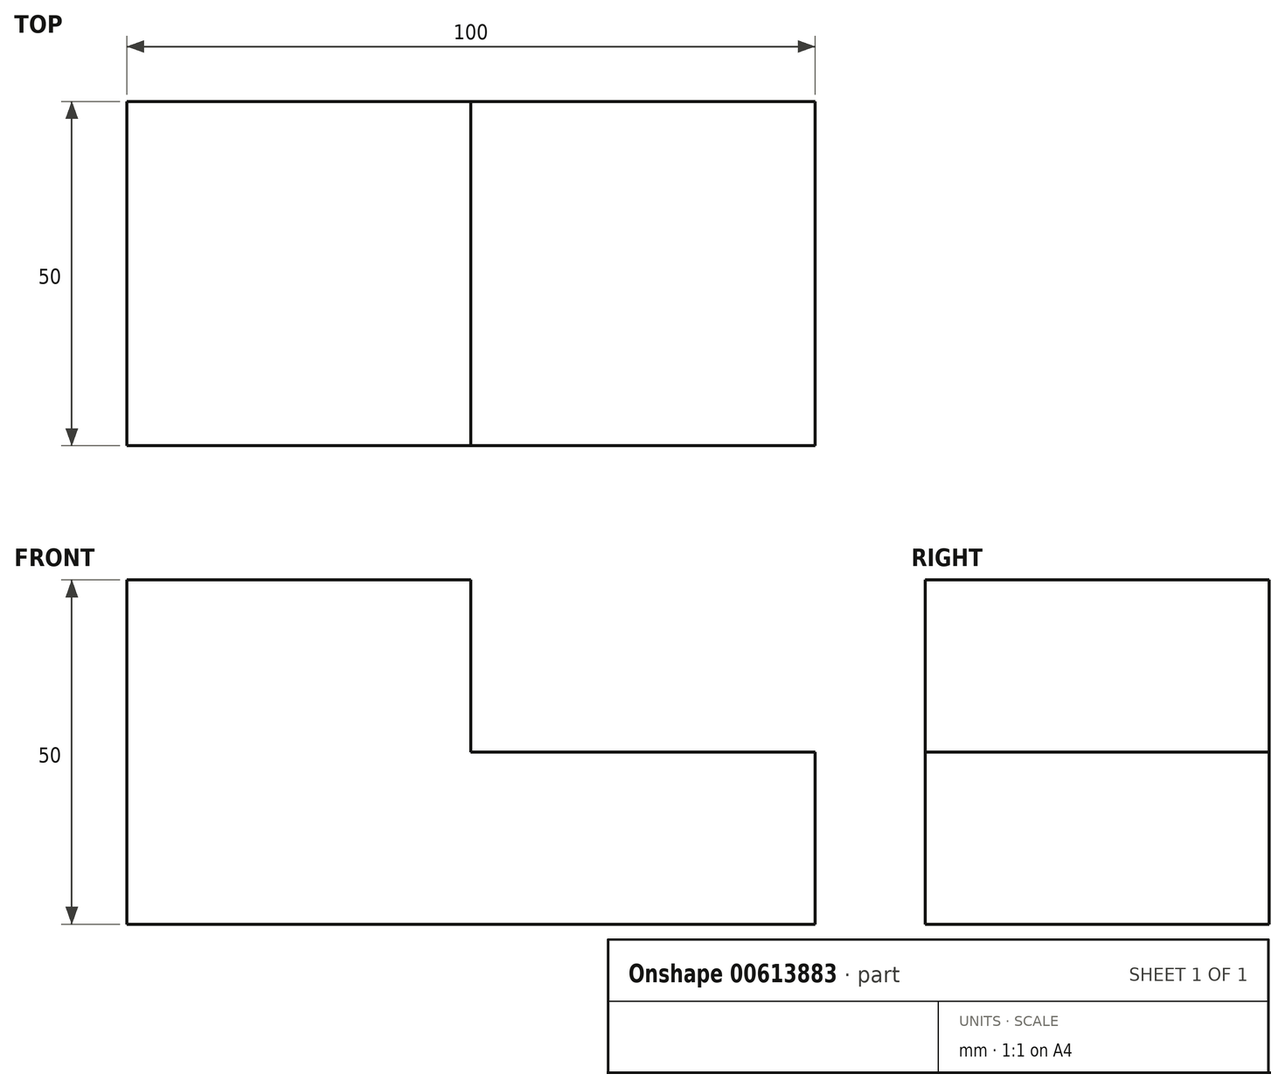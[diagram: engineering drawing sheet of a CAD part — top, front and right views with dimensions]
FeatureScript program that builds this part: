
annotation { "Feature Type Name" : "Feature", "Feature Type Description" : "" }
export const myFeature = defineFeature(function(context is Context, id is Id, definition is map)
    precondition{}
    {
        {
            var Q0;
            Q0=qCreatedBy(makeId("Front.planeOp"),FACE);
            var sketch = newSketch(context, id + "F0", { "sketchPlane" : qUnion([Q0])});
            skLineSegment(sketch, "E0", {"start": v(-45.04, 23.42) * mm, "end": v(-45.04, -26.58) * mm});
            skLineSegment(sketch, "E1", {"start": v(-45.04, -26.58) * mm, "end": v(54.96, -26.58) * mm});
            skLineSegment(sketch, "E2", {"start": v(54.96, -26.58) * mm, "end": v(54.96, -1.58) * mm});
            skLineSegment(sketch, "E3", {"start": v(54.96, -1.58) * mm, "end": v(4.96, -1.58) * mm});
            skLineSegment(sketch, "E4", {"start": v(-45.04, 23.42) * mm, "end": v(4.96, 23.42) * mm});
            skLineSegment(sketch, "E5", {"start": v(4.96, 23.42) * mm, "end": v(4.96, -1.58) * mm});
            skSolve(sketch);
        }
        {
            var Q0;
            Q0=makeQuery(id+"F0.imprint","IMPRINT",FACE,{"disambiguationData":[TD([[makeQuery(id+"F0.imprint","IMPRINT",EDGE,{"derivedFrom":sQuery(id+"F0.wireOp",EDGE,"E0")}),1.0]])]});
            extrude(context, id + "F1", {"entities" : qUnion([Q0]), "depth" : 50 * mm, "offsetDistance" : 25 * mm});
        }
    });
